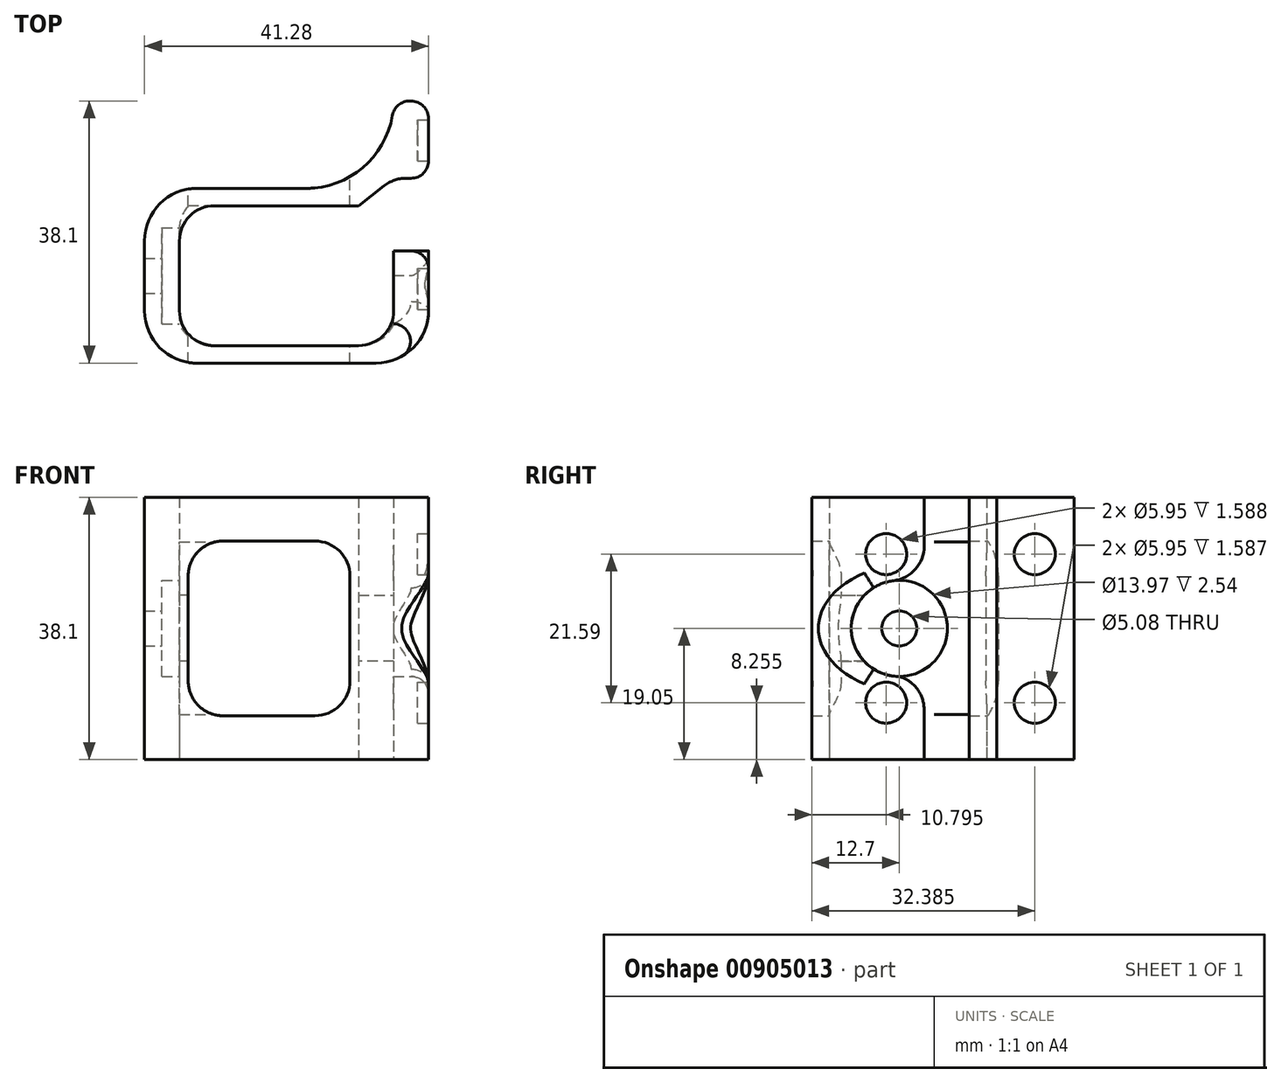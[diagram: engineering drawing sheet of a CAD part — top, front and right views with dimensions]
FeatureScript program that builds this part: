
annotation { "Feature Type Name" : "Feature", "Feature Type Description" : "" }
export const myFeature = defineFeature(function(context is Context, id is Id, definition is map)
    precondition{}
    {
        {
            var Q0;
            Q0=qCreatedBy(makeId("Top.planeOp"),FACE);
            var sketch = newSketch(context, id + "F0", { "sketchPlane" : qUnion([Q0])});
            skLineSegment(sketch, "E0.bottom", {"start": v(2.86, 12.7) * mm, "end": v(-20.64, 12.7) * mm});
            skLineSegment(sketch, "E0.top", {"start": v(20.64, -12.7) * mm, "end": v(-20.64, -12.7) * mm});
            skLineSegment(sketch, "E0.left", {"start": v(20.64, 12.7) * mm, "end": v(20.64, -12.7) * mm});
            skLineSegment(sketch, "E0.right", {"start": v(-20.64, 12.7) * mm, "end": v(-20.64, -12.7) * mm});
            skPoint(sketch, "E0.middle", {"position": v(0, 0) * mm});
            skArc(sketch, "E1", {"start": v(2.86, 12.7) * mm, "mid": v(11.84, 16.42) * mm, "end": v(15.56, 25.4) * mm});
            skLineSegment(sketch, "E2.bottom", {"start": v(15.56, 10.16) * mm, "end": v(-15.56, 10.16) * mm});
            skLineSegment(sketch, "E2.top", {"start": v(15.56, -10.16) * mm, "end": v(-15.56, -10.16) * mm});
            skLineSegment(sketch, "E2.left", {"start": v(15.56, 10.16) * mm, "end": v(15.56, -10.16) * mm});
            skLineSegment(sketch, "E2.right", {"start": v(-15.56, 10.16) * mm, "end": v(-15.56, -10.16) * mm});
            skLineSegment(sketch, "E3", {"start": v(20.64, 12.7) * mm, "end": v(20.64, 25.4) * mm});
            skLineSegment(sketch, "E4", {"start": v(20.64, 25.4) * mm, "end": v(2.86, 25.4) * mm});
            skSolve(sketch);
        }
        {
            var Q0;
            Q0 = qSketchRegion(id + "F0", true);
            extrude(context, id + "F1", {"entities" : qUnion([Q0]), "depth" : 38.1 * mm, "offsetDistance" : 25.4 * mm});
        }
        {
            var Q0;
            Q0=makeQuery(id+"F1.opExtrude","SWEPT_FACE",FACE,{"disambiguationData":[OSD([sQuery(id+"F0.wireOp",EDGE,"E2.right")])]});
            var sketch = newSketch(context, id + "F2", { "sketchPlane" : qUnion([Q0])});
            skCircle(sketch, "E5", {"center": v(0, 19.05) * mm, "radius": 6.99 * mm});
            skSolve(sketch);
        }
        {
            var Q0;
            Q0 = qSketchRegion(id + "F2", true);
            extrude(context, id + "F3", {"entities" : qUnion([Q0]), "operationType" : NewBodyOperationType.REMOVE, "oppositeDirection" : true, "depth" : 2.54 * mm, "offsetDistance" : 25.4 * mm, "hasSecondDirection" : true, "secondDirectionBound" : SecondDirectionBoundingType.THROUGH_ALL, "secondDirectionOppositeDirection" : false, "secondDirectionDepth" : 25.4 * mm});
        }
        {
            var Q0;
            Q0=makeQuery(id+"F3.boolean.opBoolean","COPY",FACE,{"derivedFrom":makeQuery(id+"F3.opExtrude","CAP_FACE",FACE,{"disambiguationData":[OSD([sQuery(id+"F2.wireOp",EDGE,"E5")])],"isStart":false})});
            var sketch = newSketch(context, id + "F4", { "sketchPlane" : qUnion([Q0])});
            skCircle(sketch, "E6", {"center": v(0, 19.05) * mm, "radius": 2.54 * mm});
            skSolve(sketch);
        }
        {
            var Q0;
            Q0 = qSketchRegion(id + "F4", true);
            extrude(context, id + "F5", {"entities" : qUnion([Q0]), "operationType" : NewBodyOperationType.REMOVE, "oppositeDirection" : true, "depth" : 25.4 * mm, "offsetDistance" : 25.4 * mm});
        }
        {
            var Q0;
            Q0=makeQuery(id+"F1.opExtrude","SWEPT_FACE",FACE,{"disambiguationData":[OSD([sQuery(id+"F0.wireOp",EDGE,"E0.bottom")])]});
            var sketch = newSketch(context, id + "F6", { "sketchPlane" : qUnion([Q0])});
            skLineSegment(sketch, "E7.bottom", {"start": v(-9.2, 31.75) * mm, "end": v(14.29, 31.75) * mm});
            skLineSegment(sketch, "E7.top", {"start": v(-9.2, 6.35) * mm, "end": v(14.29, 6.35) * mm});
            skLineSegment(sketch, "E7.left", {"start": v(-9.2, 31.75) * mm, "end": v(-9.2, 6.35) * mm});
            skLineSegment(sketch, "E7.right", {"start": v(14.29, 31.75) * mm, "end": v(14.29, 6.35) * mm});
            skPoint(sketch, "E7.middle", {"position": v(2.54, 19.05) * mm});
            skSolve(sketch);
        }
        {
            var Q0;
            Q0 = qSketchRegion(id + "F6", true);
            extrude(context, id + "F7", {"entities" : qUnion([Q0]), "operationType" : NewBodyOperationType.REMOVE, "oppositeDirection" : true, "depth" : 25.4 * mm, "offsetDistance" : 25.4 * mm, "hasSecondDirection" : true, "secondDirectionOppositeDirection" : false, "secondDirectionDepth" : 25.4 * mm});
        }
        {
            var Q0;
            {var subQ0=sQuery(id+"F6.wireOp",EDGE,"E7.left");var subQ1=sQuery(id+"F6.wireOp",EDGE,"E7.top");Q0=makeQuery(id+"F7.boolean.opBoolean","COPY",EDGE,{"disambiguationData":[TD([makeQuery(id+"F1.opExtrude","SWEPT_FACE",FACE,{"disambiguationData":[OSD([sQuery(id+"F0.wireOp",EDGE,"E1")])]})])],"derivedFrom":makeQuery(id+"F7.opExtrude","SWEPT_EDGE",EDGE,{"disambiguationData":[OSD([subQ1,subQ0])]})});}
            var Q1;
            {var subQ0=sQuery(id+"F6.wireOp",EDGE,"E7.bottom");var subQ1=sQuery(id+"F6.wireOp",EDGE,"E7.right");Q1=makeQuery(id+"F7.boolean.opBoolean","COPY",EDGE,{"disambiguationData":[TD([makeQuery(id+"F1.opExtrude","SWEPT_FACE",FACE,{"disambiguationData":[OSD([sQuery(id+"F0.wireOp",EDGE,"E0.bottom")])]})])],"derivedFrom":makeQuery(id+"F7.opExtrude","SWEPT_EDGE",EDGE,{"disambiguationData":[OSD([subQ0,subQ1])]})});}
            var Q2;
            {var subQ0=sQuery(id+"F6.wireOp",EDGE,"E7.top");var subQ1=sQuery(id+"F6.wireOp",EDGE,"E7.left");Q2=makeQuery(id+"F7.boolean.opBoolean","COPY",EDGE,{"disambiguationData":[TD([makeQuery(id+"F1.opExtrude","SWEPT_FACE",FACE,{"disambiguationData":[OSD([sQuery(id+"F0.wireOp",EDGE,"E0.top")])]})])],"derivedFrom":makeQuery(id+"F7.opExtrude","SWEPT_EDGE",EDGE,{"disambiguationData":[OSD([subQ0,subQ1])]})});}
            var Q3;
            {var subQ0=sQuery(id+"F6.wireOp",EDGE,"E7.bottom");var subQ1=sQuery(id+"F6.wireOp",EDGE,"E7.left");Q3=makeQuery(id+"F7.boolean.opBoolean","COPY",EDGE,{"disambiguationData":[TD([makeQuery(id+"F1.opExtrude","SWEPT_FACE",FACE,{"disambiguationData":[OSD([sQuery(id+"F0.wireOp",EDGE,"E0.top")])]})])],"derivedFrom":makeQuery(id+"F7.opExtrude","SWEPT_EDGE",EDGE,{"disambiguationData":[OSD([subQ0,subQ1])]})});}
            var Q4;
            {var subQ0=sQuery(id+"F6.wireOp",EDGE,"E7.left");var subQ1=sQuery(id+"F6.wireOp",EDGE,"E7.bottom");Q4=makeQuery(id+"F7.boolean.opBoolean","COPY",EDGE,{"disambiguationData":[TD([makeQuery(id+"F1.opExtrude","SWEPT_FACE",FACE,{"disambiguationData":[OSD([sQuery(id+"F0.wireOp",EDGE,"E1")])]})])],"derivedFrom":makeQuery(id+"F7.opExtrude","SWEPT_EDGE",EDGE,{"disambiguationData":[OSD([subQ1,subQ0])]})});}
            var Q5;
            Q5=makeQuery(id+"F1.opExtrude","SWEPT_EDGE",EDGE,{"disambiguationData":[OSD([sQuery(id+"F0.wireOp",EDGE,"E2.bottom"),sQuery(id+"F0.wireOp",EDGE,"E2.left")])]});
            var Q6;
            Q6=makeQuery(id+"F1.opExtrude","SWEPT_EDGE",EDGE,{"disambiguationData":[OSD([sQuery(id+"F0.wireOp",EDGE,"E2.top"),sQuery(id+"F0.wireOp",EDGE,"E2.left")])]});
            var Q7;
            Q7=makeQuery(id+"F1.opExtrude","SWEPT_EDGE",EDGE,{"disambiguationData":[OSD([sQuery(id+"F0.wireOp",EDGE,"E2.top"),sQuery(id+"F0.wireOp",EDGE,"E2.right")])]});
            fillet(context, id + "F8", {"entities" : qUnion([Q0, Q1, Q2, Q3, Q4, Q5, Q6, Q7]), "radius" : 5.08 * mm, "tangentPropagation" : true, "allowEdgeOverflow" : false});
        }
        {
            var Q0;
            {var subQ0=sQuery(id+"F6.wireOp",EDGE,"E7.top");var subQ1=sQuery(id+"F6.wireOp",EDGE,"E7.right");Q0=makeQuery(id+"F7.boolean.opBoolean","COPY",EDGE,{"disambiguationData":[TD([makeQuery(id+"F1.opExtrude","SWEPT_FACE",FACE,{"disambiguationData":[OSD([sQuery(id+"F0.wireOp",EDGE,"E0.bottom")])]})])],"derivedFrom":makeQuery(id+"F7.opExtrude","SWEPT_EDGE",EDGE,{"disambiguationData":[OSD([subQ0,subQ1])]})});}
            var Q1;
            {var subQ0=sQuery(id+"F6.wireOp",EDGE,"E7.top");var subQ1=sQuery(id+"F6.wireOp",EDGE,"E7.right");Q1=makeQuery(id+"F7.boolean.opBoolean","COPY",EDGE,{"disambiguationData":[TD([makeQuery(id+"F1.opExtrude","SWEPT_FACE",FACE,{"disambiguationData":[OSD([sQuery(id+"F0.wireOp",EDGE,"E0.top")])]})])],"derivedFrom":makeQuery(id+"F7.opExtrude","SWEPT_EDGE",EDGE,{"disambiguationData":[OSD([subQ0,subQ1])]})});}
            var Q2;
            {var subQ0=sQuery(id+"F6.wireOp",EDGE,"E7.bottom");var subQ1=sQuery(id+"F6.wireOp",EDGE,"E7.right");Q2=makeQuery(id+"F7.boolean.opBoolean","COPY",EDGE,{"disambiguationData":[TD([makeQuery(id+"F1.opExtrude","SWEPT_FACE",FACE,{"disambiguationData":[OSD([sQuery(id+"F0.wireOp",EDGE,"E0.top")])]})])],"derivedFrom":makeQuery(id+"F7.opExtrude","SWEPT_EDGE",EDGE,{"disambiguationData":[OSD([subQ0,subQ1])]})});}
            fillet(context, id + "F9", {"entities" : qUnion([Q0, Q1, Q2]), "radius" : 5.08 * mm, "tangentPropagation" : true, "allowEdgeOverflow" : false});
        }
        {
            var Q0;
            Q0=makeQuery(id+"F1.opExtrude","SWEPT_EDGE",EDGE,{"disambiguationData":[OSD([sQuery(id+"F0.wireOp",EDGE,"E2.bottom"),sQuery(id+"F0.wireOp",EDGE,"E2.right")])]});
            fillet(context, id + "F10", {"entities" : qUnion([Q0]), "radius" : 5.08 * mm, "tangentPropagation" : true, "allowEdgeOverflow" : false});
        }
        {
            var Q0;
            Q0=makeQuery(id+"F1.opExtrude","SWEPT_EDGE",EDGE,{"disambiguationData":[OSD([sQuery(id+"F0.wireOp",EDGE,"E0.top"),sQuery(id+"F0.wireOp",EDGE,"E0.left")])]});
            var Q1;
            Q1=makeQuery(id+"F1.opExtrude","SWEPT_EDGE",EDGE,{"disambiguationData":[OSD([sQuery(id+"F0.wireOp",EDGE,"E0.bottom"),sQuery(id+"F0.wireOp",EDGE,"E0.right")])]});
            var Q2;
            Q2=makeQuery(id+"F1.opExtrude","SWEPT_EDGE",EDGE,{"disambiguationData":[OSD([sQuery(id+"F0.wireOp",EDGE,"E0.top"),sQuery(id+"F0.wireOp",EDGE,"E0.right")])]});
            fillet(context, id + "F11", {"entities" : qUnion([Q0, Q1, Q2]), "radius" : 7.62 * mm, "tangentPropagation" : true, "allowEdgeOverflow" : false});
        }
        {
            var Q0;
            Q0=makeQuery(id+"F1.opExtrude","SWEPT_EDGE",EDGE,{"disambiguationData":[OSD([sQuery(id+"F0.wireOp",EDGE,"E1"),sQuery(id+"F0.wireOp",EDGE,"E4")])]});
            var Q1;
            Q1=makeQuery(id+"F1.opExtrude","SWEPT_EDGE",EDGE,{"disambiguationData":[OSD([sQuery(id+"F0.wireOp",EDGE,"E3"),sQuery(id+"F0.wireOp",EDGE,"E4")])]});
            fillet(context, id + "F12", {"entities" : qUnion([Q0, Q1]), "radius" : 2.54 * mm, "tangentPropagation" : true, "allowEdgeOverflow" : false});
        }
        {
            var Q0;
            Q0=makeQuery(id+"F1.opExtrude","SWEPT_FACE",FACE,{"disambiguationData":[OSD([sQuery(id+"F0.wireOp",EDGE,"E0.left"),sQuery(id+"F0.wireOp",EDGE,"E3")])]});
            var sketch = newSketch(context, id + "F13", { "sketchPlane" : qUnion([Q0])});
            skCircle(sketch, "E8", {"center": v(-1.9, 8.25) * mm, "radius": 2.98 * mm});
            skCircle(sketch, "E9", {"center": v(19.69, 8.25) * mm, "radius": 2.98 * mm});
            skCircle(sketch, "E10", {"center": v(-1.9, 29.84) * mm, "radius": 2.98 * mm});
            skCircle(sketch, "E11", {"center": v(19.69, 29.84) * mm, "radius": 2.98 * mm});
            skSolve(sketch);
        }
        {
            var Q0;
            Q0 = qSketchRegion(id + "F13", true);
            extrude(context, id + "F14", {"entities" : qUnion([Q0]), "operationType" : NewBodyOperationType.REMOVE, "oppositeDirection" : true, "depth" : 1.59 * mm, "offsetDistance" : 25.4 * mm});
        }
        {
            var Q0;
            Q0=makeQuery(id+"F1.opExtrude","SWEPT_FACE",FACE,{"disambiguationData":[OSD([sQuery(id+"F0.wireOp",EDGE,"E0.left"),sQuery(id+"F0.wireOp",EDGE,"E3")])]});
            var sketch = newSketch(context, id + "F15", { "sketchPlane" : qUnion([Q0])});
            skLineSegment(sketch, "E12.bottom", {"start": v(3.61, 38.1) * mm, "end": v(14.17, 38.1) * mm});
            skLineSegment(sketch, "E12.top", {"start": v(3.61, 0) * mm, "end": v(14.17, 0) * mm});
            skLineSegment(sketch, "E12.left", {"start": v(3.61, 38.1) * mm, "end": v(3.61, 0) * mm});
            skLineSegment(sketch, "E12.right", {"start": v(14.17, 38.1) * mm, "end": v(14.17, 0) * mm});
            skSolve(sketch);
        }
        {
            var Q0;
            Q0 = qSketchRegion(id + "F15", true);
            var Q1;
            {var subQ7=sQuery(id+"F15.wireOp",EDGE,"E12.bottom");Q1=makeQuery(id+"F15.imprint","IMPRINT",FACE,{"disambiguationData":[TD([[makeQuery(id+"F15.imprint","IMPRINT",EDGE,{"derivedFrom":subQ7}),-1.0]])]});}
            extrude(context, id + "F16", {"entities" : qUnion([Q0, Q1]), "operationType" : NewBodyOperationType.REMOVE, "oppositeDirection" : true, "depth" : 5.08 * mm, "offsetDistance" : 25.4 * mm});
        }
        {
            var Q0;
            Q0=makeQuery(id+"F1.opExtrude","CAP_FACE",FACE,{"disambiguationData":[OSD([sQuery(id+"F0.wireOp",EDGE,"E0.bottom"),sQuery(id+"F0.wireOp",EDGE,"E0.top"),sQuery(id+"F0.wireOp",EDGE,"E0.left"),sQuery(id+"F0.wireOp",EDGE,"E0.right"),sQuery(id+"F0.wireOp",EDGE,"E1"),sQuery(id+"F0.wireOp",EDGE,"E2.bottom"),sQuery(id+"F0.wireOp",EDGE,"E2.top"),sQuery(id+"F0.wireOp",EDGE,"E2.left"),sQuery(id+"F0.wireOp",EDGE,"E2.right"),sQuery(id+"F0.wireOp",EDGE,"E3"),sQuery(id+"F0.wireOp",EDGE,"E4")])],"isStart":true});
            var sketch = newSketch(context, id + "F17", { "sketchPlane" : qUnion([Q0])});
            skLineSegment(sketch, "E13", {"start": v(15.56, -14.17) * mm, "end": v(10.48, -10.16) * mm});
            skSolve(sketch);
        }
        {
            var Q0;
            {var subQ0=sQuery(id+"F0.wireOp",EDGE,"E0.left");var subQ2=sQuery(id+"F0.wireOp",EDGE,"E3");var subQ3=makeQuery(id+"F1.opExtrude","SWEPT_FACE",FACE,{"disambiguationData":[OSD([subQ0,subQ2])]});Q0=makeQuery(id+"F16.boolean.opBoolean","SPLIT",FACE,{"disambiguationData":[TD([makeQuery(id+"F14.boolean.opBoolean","COPY",FACE,{"derivedFrom":makeQuery(id+"F14.opExtrude","SWEPT_FACE",FACE,{"disambiguationData":[OSD([sQuery(id+"F13.wireOp",EDGE,"E10")])]})})])],"derivedFrom":subQ3});}
            var sketch = newSketch(context, id + "F18", { "sketchPlane" : qUnion([Q0])});
            skLineSegment(sketch, "E14.bottom", {"start": v(0.02, 26.03) * mm, "end": v(7.64, 26.03) * mm});
            skLineSegment(sketch, "E14.top", {"start": v(0.02, 12.06) * mm, "end": v(7.64, 12.06) * mm});
            skLineSegment(sketch, "E14.left", {"start": v(0.02, 26.03) * mm, "end": v(0.02, 12.06) * mm});
            skLineSegment(sketch, "E14.right", {"start": v(7.64, 26.03) * mm, "end": v(7.64, 12.06) * mm});
            skSolve(sketch);
        }
        {
            var Q0;
            Q0=makeQuery(id+"F17.imprint","IMPRINT",FACE,{"disambiguationData":[TD([[makeQuery(id+"F17.imprint","IMPRINT",EDGE,{"derivedFrom":sQuery(id+"F17.wireOp",EDGE,"E13")}),-1.0]])]});
            extrude(context, id + "F19", {"entities" : qUnion([Q0]), "operationType" : NewBodyOperationType.REMOVE, "endBound" : BoundingType.THROUGH_ALL, "oppositeDirection" : true, "depth" : 25.4 * mm, "offsetDistance" : 25.4 * mm});
        }
        {
            var Q0;
            Q0=makeQuery(id+"F18.imprint","IMPRINT",FACE,{"disambiguationData":[TD([[makeQuery(id+"F18.imprint","IMPRINT",EDGE,{"derivedFrom":sQuery(id+"F18.wireOp",EDGE,"E14.top")}),1.0]])]});
            var Q1;
            {var subQ0=sQuery(id+"F18.wireOp",EDGE,"E14.bottom");var subQ1=makeQuery(id+"F3.opExtrude","SWEPT_FACE",FACE,{"disambiguationData":[OSD([sQuery(id+"F2.wireOp",EDGE,"E5")])]});var subQ2=sQuery(id+"F0.wireOp",EDGE,"E3");var subQ3=sQuery(id+"F0.wireOp",EDGE,"E0.left");var subQ4=makeQuery(id+"F1.opExtrude","SWEPT_FACE",FACE,{"disambiguationData":[OSD([subQ3,subQ2])]});var subQ5=makeQuery(id+"F16.boolean.opBoolean","SPLIT",EDGE,{"disambiguationData":[OD(1.0)],"derivedFrom":makeQuery(id+"F3.boolean.opBoolean","INTERSECT",EDGE,{"derivedFrom":[subQ4,subQ1]})});var subQ6=makeQuery(id+"F18.imprint","INTERSECT",VERTEX,{"derivedFrom":[subQ5,subQ0,sQuery(id+"F18.wireOp",EDGE,"E14.left")]});Q1=makeQuery(id+"F18.imprint","IMPRINT",FACE,{"disambiguationData":[TD([[makeQuery(id+"F18.imprint","IMPRINT",EDGE,{"disambiguationData":[TD([[subQ6,-1.0]])],"derivedFrom":subQ0}),-1.0]])]});}
            extrude(context, id + "F20", {"entities" : qUnion([Q0, Q1]), "operationType" : NewBodyOperationType.REMOVE, "oppositeDirection" : true, "depth" : 25.4 * mm, "offsetDistance" : 25.4 * mm});
        }
        {
            var Q0;
            {var subQ0=sQuery(id+"F0.wireOp",EDGE,"E3");var subQ1=sQuery(id+"F0.wireOp",EDGE,"E2.left");var subQ2=sQuery(id+"F0.wireOp",EDGE,"E0.left");Q0=makeQuery(id+"F20.boolean.opBoolean","INTERSECT",EDGE,{"derivedFrom":[makeQuery(id+"F16.boolean.opBoolean","COPY",FACE,{"disambiguationData":[TD([makeQuery(id+"F1.opExtrude","CAP_FACE",FACE,{"disambiguationData":[OSD([sQuery(id+"F0.wireOp",EDGE,"E0.bottom"),sQuery(id+"F0.wireOp",EDGE,"E0.top"),subQ2,sQuery(id+"F0.wireOp",EDGE,"E0.right"),sQuery(id+"F0.wireOp",EDGE,"E1"),sQuery(id+"F0.wireOp",EDGE,"E2.bottom"),sQuery(id+"F0.wireOp",EDGE,"E2.top"),subQ1,sQuery(id+"F0.wireOp",EDGE,"E2.right"),subQ0,sQuery(id+"F0.wireOp",EDGE,"E4")])],"isStart":true})])],"derivedFrom":makeQuery(id+"F16.opExtrude","SWEPT_FACE",FACE,{"disambiguationData":[OSD([sQuery(id+"F15.wireOp",EDGE,"E12.left")])]})}),makeQuery(id+"F20.opExtrude","SWEPT_FACE",FACE,{"disambiguationData":[OSD([sQuery(id+"F18.wireOp",EDGE,"E14.top")])]})]});}
            var Q1;
            {var subQ0=sQuery(id+"F0.wireOp",EDGE,"E3");var subQ1=sQuery(id+"F0.wireOp",EDGE,"E2.left");var subQ2=sQuery(id+"F0.wireOp",EDGE,"E0.left");Q1=makeQuery(id+"F20.boolean.opBoolean","INTERSECT",EDGE,{"derivedFrom":[makeQuery(id+"F16.boolean.opBoolean","COPY",FACE,{"disambiguationData":[TD([makeQuery(id+"F1.opExtrude","CAP_FACE",FACE,{"disambiguationData":[OSD([sQuery(id+"F0.wireOp",EDGE,"E0.bottom"),sQuery(id+"F0.wireOp",EDGE,"E0.top"),subQ2,sQuery(id+"F0.wireOp",EDGE,"E0.right"),sQuery(id+"F0.wireOp",EDGE,"E1"),sQuery(id+"F0.wireOp",EDGE,"E2.bottom"),sQuery(id+"F0.wireOp",EDGE,"E2.top"),subQ1,sQuery(id+"F0.wireOp",EDGE,"E2.right"),subQ0,sQuery(id+"F0.wireOp",EDGE,"E4")])],"isStart":false})])],"derivedFrom":makeQuery(id+"F16.opExtrude","SWEPT_FACE",FACE,{"disambiguationData":[OSD([sQuery(id+"F15.wireOp",EDGE,"E12.left")])]})}),makeQuery(id+"F20.opExtrude","SWEPT_FACE",FACE,{"disambiguationData":[OSD([sQuery(id+"F18.wireOp",EDGE,"E14.bottom")])]})]});}
            fillet(context, id + "F21", {"entities" : qUnion([Q0, Q1]), "radius" : 5.08 * mm, "tangentPropagation" : true, "allowEdgeOverflow" : false});
        }
        {
            var Q0;
            {var subQ0=sQuery(id+"F0.wireOp",EDGE,"E2.left");var subQ1=sQuery(id+"F0.wireOp",EDGE,"E2.bottom");var subQ2=makeQuery(id+"F1.opExtrude","SWEPT_FACE",FACE,{"disambiguationData":[OSD([subQ1])]});var subQ3=makeQuery(id+"F1.opExtrude","SWEPT_EDGE",EDGE,{"disambiguationData":[OSD([subQ1,subQ0])]});Q0=makeQuery(id+"F19.boolean.opBoolean","MERGE",EDGE,{"derivedFrom":[makeQuery(id+"F8.opFillet","BLEND_EDGE",EDGE,{"disambiguationData":[OD(0.0)],"blendedFrom":[subQ3,subQ2],"blendedInto":[subQ2]}),makeQuery(id+"F8.opFillet","BLEND_EDGE",EDGE,{"disambiguationData":[OD(1.0)],"blendedFrom":[subQ3,subQ2],"blendedInto":[subQ2]})],"fromTools":[makeQuery(id+"F19.opExtrude","SWEPT_EDGE",EDGE,{"disambiguationData":[OSD([sQuery(id+"F0.wireOp",EDGE,"E0.bottom"),sQuery(id+"F0.wireOp",EDGE,"E0.top"),sQuery(id+"F0.wireOp",EDGE,"E0.left"),sQuery(id+"F0.wireOp",EDGE,"E0.right"),sQuery(id+"F0.wireOp",EDGE,"E1"),subQ1,sQuery(id+"F0.wireOp",EDGE,"E2.top"),subQ0,sQuery(id+"F0.wireOp",EDGE,"E2.right"),sQuery(id+"F0.wireOp",EDGE,"E3"),sQuery(id+"F0.wireOp",EDGE,"E4"),sQuery(id+"F17.wireOp",EDGE,"E13")])]})]});}
            var Q1;
            {var subQ0=sQuery(id+"F15.wireOp",EDGE,"E12.right");Q1=makeQuery(id+"F19.boolean.opBoolean","MERGE",EDGE,{"derivedFrom":[makeQuery(id+"F16.boolean.opBoolean","COPY",EDGE,{"derivedFrom":makeQuery(id+"F16.opExtrude","CAP_EDGE",EDGE,{"disambiguationData":[OSD([subQ0])],"isStart":false})})],"fromTools":[makeQuery(id+"F19.opExtrude","SWEPT_EDGE",EDGE,{"disambiguationData":[OSD([sQuery(id+"F0.wireOp",EDGE,"E0.left"),sQuery(id+"F0.wireOp",EDGE,"E3"),sQuery(id+"F15.wireOp",EDGE,"E12.top"),subQ0,sQuery(id+"F17.wireOp",EDGE,"E13")])]})]});}
            fillet(context, id + "F22", {"entities" : qUnion([Q0, Q1]), "radius" : 5.08 * mm, "tangentPropagation" : true, "allowEdgeOverflow" : false});
        }
        {
            var Q0;
            {var subQ0=sQuery(id+"F0.wireOp",EDGE,"E3");var subQ1=sQuery(id+"F0.wireOp",EDGE,"E2.left");var subQ2=sQuery(id+"F0.wireOp",EDGE,"E0.left");var subQ4=sQuery(id+"F15.wireOp",EDGE,"E12.left");Q0=makeQuery(id+"F16.boolean.opBoolean","COPY",EDGE,{"disambiguationData":[TD([makeQuery(id+"F1.opExtrude","CAP_FACE",FACE,{"disambiguationData":[OSD([sQuery(id+"F0.wireOp",EDGE,"E0.bottom"),sQuery(id+"F0.wireOp",EDGE,"E0.top"),subQ2,sQuery(id+"F0.wireOp",EDGE,"E0.right"),sQuery(id+"F0.wireOp",EDGE,"E1"),sQuery(id+"F0.wireOp",EDGE,"E2.bottom"),sQuery(id+"F0.wireOp",EDGE,"E2.top"),subQ1,sQuery(id+"F0.wireOp",EDGE,"E2.right"),subQ0,sQuery(id+"F0.wireOp",EDGE,"E4")])],"isStart":true})])],"derivedFrom":makeQuery(id+"F16.opExtrude","CAP_EDGE",EDGE,{"disambiguationData":[OSD([subQ4])],"isStart":true})});}
            var Q1;
            Q1=makeQuery(id+"F16.boolean.opBoolean","COPY",EDGE,{"derivedFrom":makeQuery(id+"F16.opExtrude","CAP_EDGE",EDGE,{"disambiguationData":[OSD([sQuery(id+"F15.wireOp",EDGE,"E12.right")])],"isStart":true})});
            var Q2;
            {var subQ0=sQuery(id+"F0.wireOp",EDGE,"E3");var subQ1=sQuery(id+"F0.wireOp",EDGE,"E2.left");var subQ2=sQuery(id+"F0.wireOp",EDGE,"E0.left");var subQ4=sQuery(id+"F15.wireOp",EDGE,"E12.left");Q2=makeQuery(id+"F16.boolean.opBoolean","COPY",EDGE,{"disambiguationData":[TD([makeQuery(id+"F1.opExtrude","CAP_FACE",FACE,{"disambiguationData":[OSD([sQuery(id+"F0.wireOp",EDGE,"E0.bottom"),sQuery(id+"F0.wireOp",EDGE,"E0.top"),subQ2,sQuery(id+"F0.wireOp",EDGE,"E0.right"),sQuery(id+"F0.wireOp",EDGE,"E1"),sQuery(id+"F0.wireOp",EDGE,"E2.bottom"),sQuery(id+"F0.wireOp",EDGE,"E2.top"),subQ1,sQuery(id+"F0.wireOp",EDGE,"E2.right"),subQ0,sQuery(id+"F0.wireOp",EDGE,"E4")])],"isStart":false})])],"derivedFrom":makeQuery(id+"F16.opExtrude","CAP_EDGE",EDGE,{"disambiguationData":[OSD([subQ4])],"isStart":true})});}
            var Q3;
            {var subQ0=sQuery(id+"F0.wireOp",EDGE,"E3");var subQ1=sQuery(id+"F0.wireOp",EDGE,"E2.left");var subQ2=sQuery(id+"F0.wireOp",EDGE,"E0.left");var subQ4=sQuery(id+"F15.wireOp",EDGE,"E12.left");Q3=makeQuery(id+"F16.boolean.opBoolean","COPY",EDGE,{"disambiguationData":[TD([makeQuery(id+"F1.opExtrude","CAP_FACE",FACE,{"disambiguationData":[OSD([sQuery(id+"F0.wireOp",EDGE,"E0.bottom"),sQuery(id+"F0.wireOp",EDGE,"E0.top"),subQ2,sQuery(id+"F0.wireOp",EDGE,"E0.right"),sQuery(id+"F0.wireOp",EDGE,"E1"),sQuery(id+"F0.wireOp",EDGE,"E2.bottom"),sQuery(id+"F0.wireOp",EDGE,"E2.top"),subQ1,sQuery(id+"F0.wireOp",EDGE,"E2.right"),subQ0,sQuery(id+"F0.wireOp",EDGE,"E4")])],"isStart":true})])],"derivedFrom":makeQuery(id+"F16.opExtrude","CAP_EDGE",EDGE,{"disambiguationData":[OSD([subQ4])],"isStart":false})});}
            var Q4;
            {var subQ0=sQuery(id+"F0.wireOp",EDGE,"E3");var subQ1=sQuery(id+"F0.wireOp",EDGE,"E2.left");var subQ2=sQuery(id+"F0.wireOp",EDGE,"E0.left");var subQ4=sQuery(id+"F15.wireOp",EDGE,"E12.left");Q4=makeQuery(id+"F16.boolean.opBoolean","COPY",EDGE,{"disambiguationData":[TD([makeQuery(id+"F1.opExtrude","CAP_FACE",FACE,{"disambiguationData":[OSD([sQuery(id+"F0.wireOp",EDGE,"E0.bottom"),sQuery(id+"F0.wireOp",EDGE,"E0.top"),subQ2,sQuery(id+"F0.wireOp",EDGE,"E0.right"),sQuery(id+"F0.wireOp",EDGE,"E1"),sQuery(id+"F0.wireOp",EDGE,"E2.bottom"),sQuery(id+"F0.wireOp",EDGE,"E2.top"),subQ1,sQuery(id+"F0.wireOp",EDGE,"E2.right"),subQ0,sQuery(id+"F0.wireOp",EDGE,"E4")])],"isStart":false})])],"derivedFrom":makeQuery(id+"F16.opExtrude","CAP_EDGE",EDGE,{"disambiguationData":[OSD([subQ4])],"isStart":false})});}
            fillet(context, id + "F23", {"entities" : qUnion([Q0, Q1, Q2, Q3, Q4]), "radius" : 2.54 * mm, "tangentPropagation" : true, "allowEdgeOverflow" : false});
        }
    });
